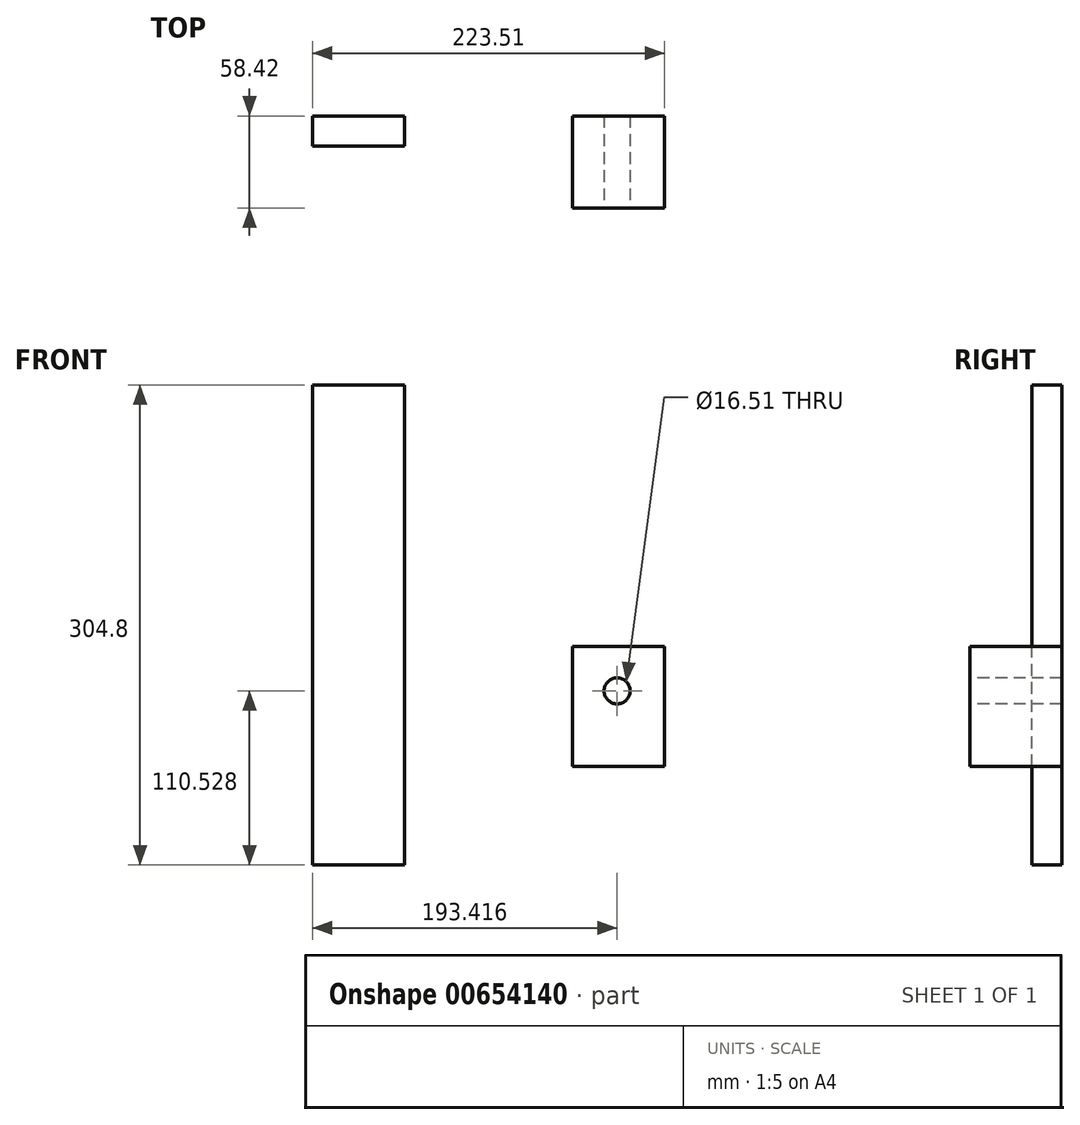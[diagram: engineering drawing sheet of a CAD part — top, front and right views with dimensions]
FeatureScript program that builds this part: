
annotation { "Feature Type Name" : "Feature", "Feature Type Description" : "" }
export const myFeature = defineFeature(function(context is Context, id is Id, definition is map)
    precondition{}
    {
        {
            var Q0;
            Q0=qCreatedBy(makeId("Front.planeOp"),FACE);
            var sketch = newSketch(context, id + "F0", { "sketchPlane" : qUnion([Q0])});
            skLineSegment(sketch, "E0", {"start": v(-47.05, 50.48) * mm, "end": v(11.37, 50.48) * mm});
            skLineSegment(sketch, "E1", {"start": v(11.37, 50.48) * mm, "end": v(11.37, -25.72) * mm});
            skLineSegment(sketch, "E2", {"start": v(11.37, -25.72) * mm, "end": v(-47.05, -25.72) * mm});
            skLineSegment(sketch, "E3", {"start": v(-47.05, -25.72) * mm, "end": v(-47.05, 50.48) * mm});
            skLineSegment(sketch, "E4", {"start": v(-212.14, -88.37) * mm, "end": v(-153.72, -88.37) * mm});
            skLineSegment(sketch, "E5", {"start": v(-153.72, -88.37) * mm, "end": v(-153.72, 216.43) * mm});
            skLineSegment(sketch, "E6", {"start": v(-153.72, 216.43) * mm, "end": v(-212.14, 216.43) * mm});
            skLineSegment(sketch, "E7", {"start": v(-212.14, 216.43) * mm, "end": v(-212.14, -88.37) * mm});
            skSolve(sketch);
        }
        {
            var Q0;
            Q0=makeQuery(id+"F0.imprint","IMPRINT",FACE,{"disambiguationData":[TD([[makeQuery(id+"F0.imprint","IMPRINT",EDGE,{"derivedFrom":sQuery(id+"F0.wireOp",EDGE,"E0")}),-1.0]])]});
            extrude(context, id + "F1", {"entities" : qUnion([Q0]), "depth" : 58.42 * mm, "offsetDistance" : 25.4 * mm});
        }
        {
            var Q0;
            Q0=makeQuery(id+"F1.opExtrude","CAP_FACE",FACE,{"disambiguationData":[OSD([sQuery(id+"F0.wireOp",EDGE,"E0"),sQuery(id+"F0.wireOp",EDGE,"E1"),sQuery(id+"F0.wireOp",EDGE,"E2"),sQuery(id+"F0.wireOp",EDGE,"E3")])],"isStart":false});
            var sketch = newSketch(context, id + "F2", { "sketchPlane" : qUnion([Q0])});
            skCircle(sketch, "E8", {"center": v(-18.72, 22.16) * mm, "radius": 8.26 * mm});
            skSolve(sketch);
        }
        {
            var Q0;
            Q0=makeQuery(id+"F2.imprint","IMPRINT",FACE,{"disambiguationData":[TD([[makeQuery(id+"F2.imprint","IMPRINT",EDGE,{"derivedFrom":sQuery(id+"F2.wireOp",EDGE,"E8")}),1.0]])]});
            extrude(context, id + "F3", {"entities" : qUnion([Q0]), "operationType" : NewBodyOperationType.REMOVE, "endBound" : BoundingType.THROUGH_ALL, "oppositeDirection" : true, "depth" : 25.4 * mm, "offsetDistance" : 25.4 * mm});
        }
        {
            var Q0;
            Q0=makeQuery(id+"F0.imprint","IMPRINT",FACE,{"disambiguationData":[TD([[makeQuery(id+"F0.imprint","IMPRINT",EDGE,{"derivedFrom":sQuery(id+"F0.wireOp",EDGE,"E4")}),1.0]])]});
            extrude(context, id + "F4", {"entities" : qUnion([Q0]), "depth" : 19.05 * mm, "offsetDistance" : 25.4 * mm});
        }
    });
